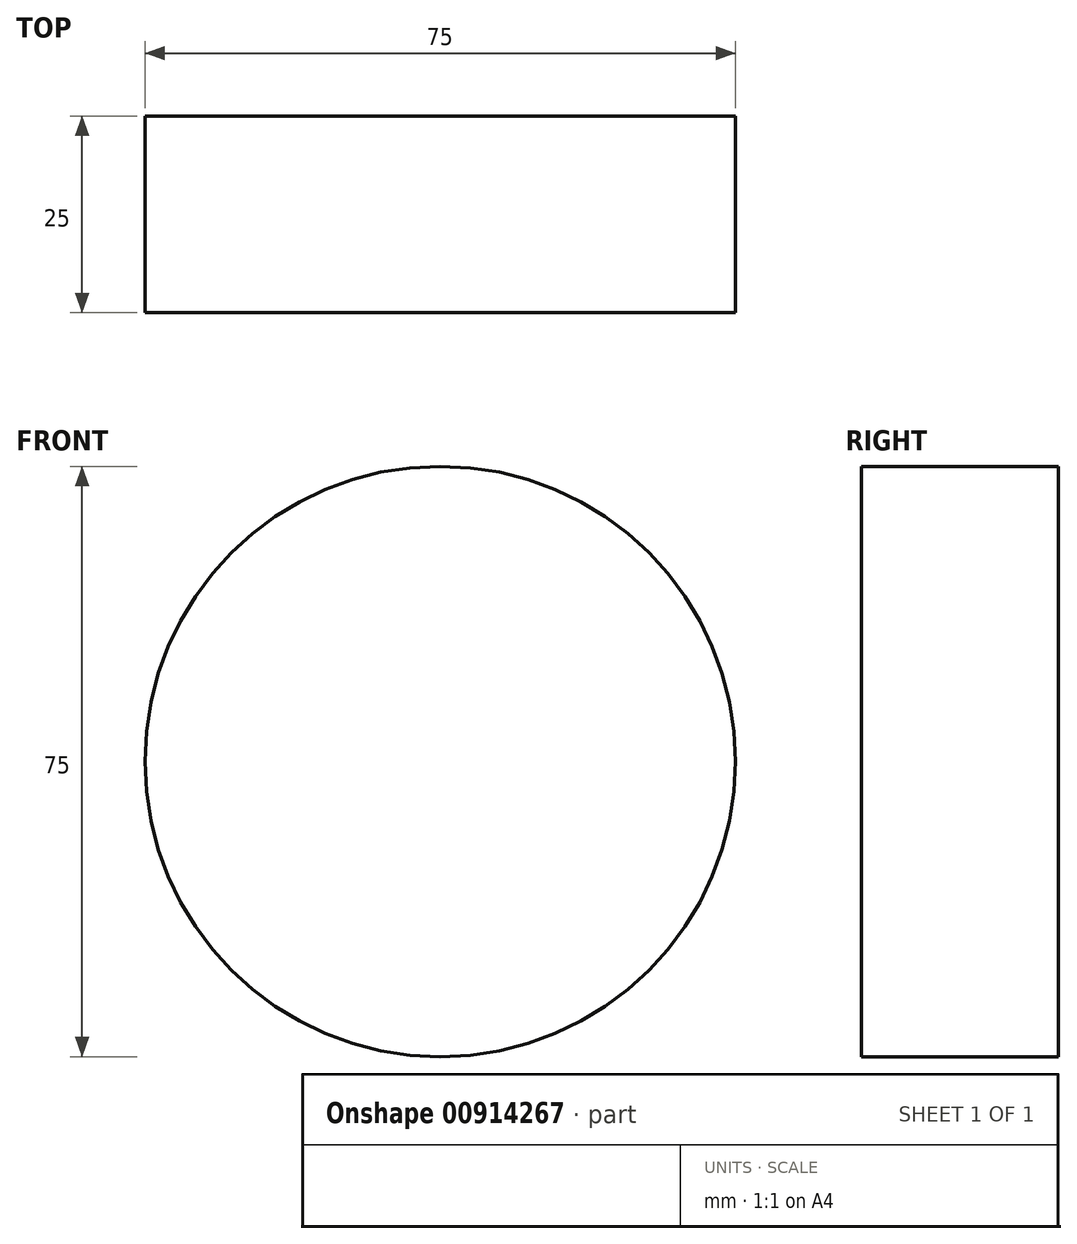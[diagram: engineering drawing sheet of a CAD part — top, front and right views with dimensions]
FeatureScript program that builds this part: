
annotation { "Feature Type Name" : "Feature", "Feature Type Description" : "" }
export const myFeature = defineFeature(function(context is Context, id is Id, definition is map)
    precondition{}
    {
        {
            var Q0;
            Q0=qCreatedBy(makeId("Front.planeOp"),FACE);
            var sketch = newSketch(context, id + "F0", { "sketchPlane" : qUnion([Q0])});
            skCircle(sketch, "E0", {"center": v(0, 0) * mm, "radius": 37.5 * mm});
            skLineSegment(sketch, "E1", {"start": v(-37.5, 0) * mm, "end": v(37.5, 0) * mm});
            skSolve(sketch);
        }
        {
            var Q0;
            {var subQ0=sQuery(id+"F0.wireOp",EDGE,"E1");Q0=makeQuery(id+"F0.imprint","IMPRINT",FACE,{"disambiguationData":[TD([[makeQuery(id+"F0.imprint","IMPRINT",EDGE,{"derivedFrom":subQ0}),-1.0]])]});}
            var Q1;
            {var subQ0=sQuery(id+"F0.wireOp",EDGE,"E1");Q1=makeQuery(id+"F0.imprint","IMPRINT",FACE,{"disambiguationData":[TD([[makeQuery(id+"F0.imprint","IMPRINT",EDGE,{"derivedFrom":subQ0}),1.0]])]});}
            extrude(context, id + "F1", {"entities" : qUnion([Q0, Q1]), "depth" : 25 * mm, "offsetDistance" : 25 * mm});
        }
    });
